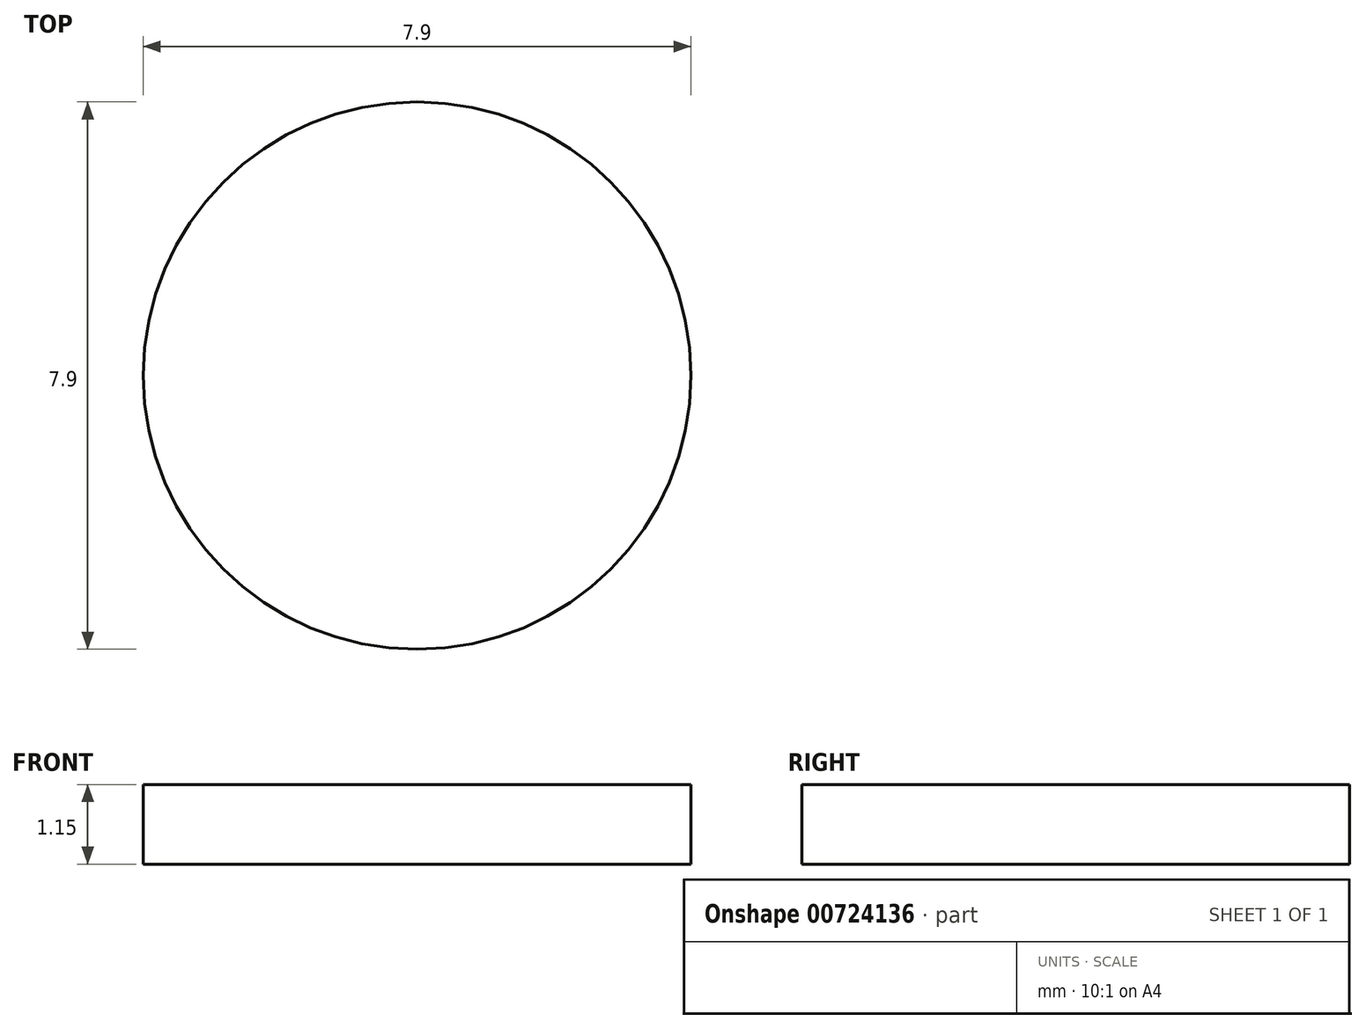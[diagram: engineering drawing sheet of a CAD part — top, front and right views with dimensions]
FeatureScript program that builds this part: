
annotation { "Feature Type Name" : "Feature", "Feature Type Description" : "" }
export const myFeature = defineFeature(function(context is Context, id is Id, definition is map)
    precondition{}
    {
        {
            var Q0;
            Q0=qCreatedBy(makeId("Top.planeOp"),FACE);
            var sketch = newSketch(context, id + "F0", { "sketchPlane" : qUnion([Q0])});
            skCircle(sketch, "E0", {"center": v(0, 0) * mm, "radius": 3.95 * mm});
            skSolve(sketch);
        }
        {
            var Q0;
            Q0=makeQuery(id+"F0.imprint","IMPRINT",FACE,{"disambiguationData":[TD([[makeQuery(id+"F0.imprint","IMPRINT",EDGE,{"derivedFrom":sQuery(id+"F0.wireOp",EDGE,"E0")}),1.0]])]});
            extrude(context, id + "F1", {"entities" : qUnion([Q0]), "depth" : ((3.3 / 2) - .2 - .3) * mm, "offsetDistance" : 25 * mm});
        }
    });
